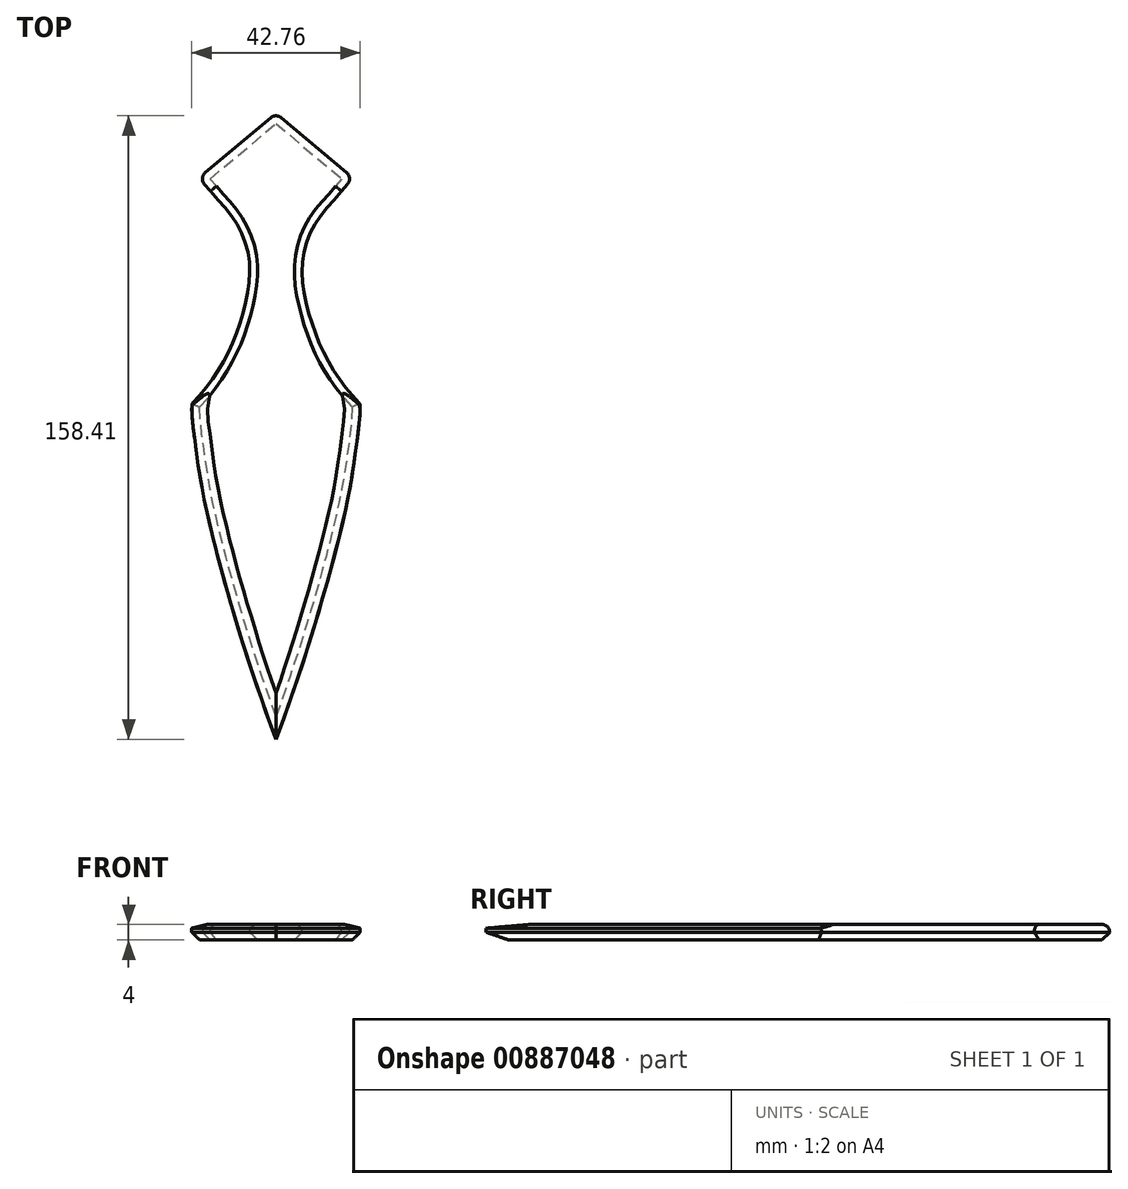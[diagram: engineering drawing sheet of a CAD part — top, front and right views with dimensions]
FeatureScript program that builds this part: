
annotation { "Feature Type Name" : "Feature", "Feature Type Description" : "" }
export const myFeature = defineFeature(function(context is Context, id is Id, definition is map)
    precondition{}
    {
        {
            var Q0;
            Q0=qCreatedBy(makeId("Top.planeOp"),FACE);
            var sketch = newSketch(context, id + "F0", { "sketchPlane" : qUnion([Q0])});
            skLineSegment(sketch, "E0", {"start": v(0, 73.74) * mm, "end": v(19.51, 57.36) * mm});
            skFitSpline(sketch, "E1", {"points": [v(21.28, 0) * mm, v(20.35, -11.32) * mm, v(18.64, -22.28) * mm, v(15.2, -37.21) * mm, v(9.92, -55.97) * mm, v(0, -85.29) * mm], "startDerivative": vector(6.55, -38.74) * mm, "endDerivative": vector(-49.45, -132.4) * mm});
            skLineSegment(sketch, "E2.MirrorCS", {"start": v(0, 73.74) * mm, "end": v(-19.51, 57.36) * mm});
            skFitSpline(sketch, "E3.MirrorCS", {"points": [v(-21.28, 0) * mm, v(-20.35, -11.32) * mm, v(-18.64, -22.28) * mm, v(-15.2, -37.21) * mm, v(-9.92, -55.97) * mm, v(0, -85.29) * mm], "startDerivative": vector(-6.55, -38.74) * mm, "endDerivative": vector(49.45, -132.4) * mm});
            skLineSegment(sketch, "E4", {"start": v(19.51, 57.36) * mm, "end": v(15.6, 57.36) * mm});
            skLineSegment(sketch, "E5", {"start": v(19.51, 57.36) * mm, "end": v(16.67, 53.97) * mm});
            skFitSpline(sketch, "E6", {"points": [v(16.67, 53.97) * mm, v(15.24, 52.32) * mm, v(10.12, 45.98) * mm, v(6.8, 36.24) * mm, v(7.63, 25.91) * mm, v(11.54, 14.16) * mm, v(16.67, 5.5) * mm, v(21.28, 0) * mm], "startDerivative": vector(-14.55, -18.2) * mm, "endDerivative": vector(34.92, -38.87) * mm});
            skLineSegment(sketch, "E7.MirrorCS", {"start": v(-19.51, 57.36) * mm, "end": v(-16.67, 53.97) * mm});
            skFitSpline(sketch, "E8.MirrorCS", {"points": [v(-16.67, 53.97) * mm, v(-15.24, 52.32) * mm, v(-10.12, 45.98) * mm, v(-6.8, 36.24) * mm, v(-7.63, 25.91) * mm, v(-11.54, 14.16) * mm, v(-16.67, 5.5) * mm, v(-21.28, 0) * mm], "startDerivative": vector(14.55, -18.2) * mm, "endDerivative": vector(-34.92, -38.87) * mm});
            skSolve(sketch);
        }
        {
            var Q0;
            Q0 = qSketchRegion(id + "F0", true);
            extrude(context, id + "F1", {"entities" : qUnion([Q0]), "depth" : 4 * mm, "offsetDistance" : 25 * mm});
        }
        {
            var Q0;
            Q0=makeQuery(id+"F1.opExtrude","SWEPT_EDGE",EDGE,{"disambiguationData":[OSD([sQuery(id+"F0.wireOp",EDGE,"E0"),sQuery(id+"F0.wireOp",EDGE,"E2.MirrorCS")])]});
            var Q1;
            Q1=makeQuery(id+"F1.opExtrude","SWEPT_EDGE",EDGE,{"disambiguationData":[OSD([sQuery(id+"F0.wireOp",EDGE,"E0"),sQuery(id+"F0.wireOp",EDGE,"E5")])]});
            var Q2;
            Q2=makeQuery(id+"F1.opExtrude","SWEPT_EDGE",EDGE,{"disambiguationData":[OSD([sQuery(id+"F0.wireOp",EDGE,"E2.MirrorCS"),sQuery(id+"F0.wireOp",EDGE,"E7.MirrorCS")])]});
            fillet(context, id + "F2", {"entities" : qUnion([Q0, Q1, Q2]), "tangentPropagation" : true, "radius" : 2 * mm, "defaultsChanged" : false, "vertexSettings" : [], "allowEdgeOverflow" : false});
        }
        {
            var Q0;
            Q0=makeQuery(id+"F1.opExtrude","CAP_FACE",FACE,{"disambiguationData":[OSD([sQuery(id+"F0.wireOp",EDGE,"E0"),sQuery(id+"F0.wireOp",EDGE,"223ab6cf-2717-4cb8-a3a4-93abdf2f02d5"),sQuery(id+"F0.wireOp",EDGE,"E1"),sQuery(id+"F0.wireOp",EDGE,"E2.MirrorCS"),sQuery(id+"F0.wireOp",EDGE,"08c7ee87-7280-4ebf-840d-ba22bd77c0a61.MirrorCS"),sQuery(id+"F0.wireOp",EDGE,"E3.MirrorCS")])],"isStart":true});
            chamfer(context, id + "F3", {"entities" : qUnion([Q0]), "width" : 2 * mm, "tangentPropagation" : true});
        }
        {
            var Q0;
            Q0=makeQuery(id+"F1.opExtrude","CAP_EDGE",EDGE,{"disambiguationData":[OSD([sQuery(id+"F0.wireOp",EDGE,"E1")])],"isStart":false});
            var Q1;
            Q1=makeQuery(id+"F1.opExtrude","CAP_EDGE",EDGE,{"disambiguationData":[OSD([sQuery(id+"F0.wireOp",EDGE,"E3.MirrorCS")])],"isStart":false});
            chamfer(context, id + "F4", {"entities" : qUnion([Q0, Q1]), "chamferType" : ChamferType.TWO_OFFSETS, "width1" : 1 * mm, "oppositeDirection" : false, "width2" : 4 * mm, "tangentPropagation" : true});
        }
        {
            var Q0;
            Q0=makeQuery(id+"F1.opExtrude","CAP_EDGE",EDGE,{"disambiguationData":[OSD([sQuery(id+"F0.wireOp",EDGE,"E6")])],"isStart":false});
            var Q1;
            {var subQ0=sQuery(id+"F0.wireOp",EDGE,"E5");var subQ1=sQuery(id+"F0.wireOp",EDGE,"E0");Q1=makeQuery(id+"F2.opFillet","BLEND_EDGE",EDGE,{"blendedFrom":[makeQuery(id+"F1.opExtrude","SWEPT_EDGE",EDGE,{"disambiguationData":[OSD([subQ1,subQ0])]}),makeQuery(id+"F1.opExtrude","CAP_FACE",FACE,{"disambiguationData":[OSD([subQ1,sQuery(id+"F0.wireOp",EDGE,"E1"),sQuery(id+"F0.wireOp",EDGE,"E2.MirrorCS"),sQuery(id+"F0.wireOp",EDGE,"E3.MirrorCS"),subQ0,sQuery(id+"F0.wireOp",EDGE,"E6"),sQuery(id+"F0.wireOp",EDGE,"E7.MirrorCS"),sQuery(id+"F0.wireOp",EDGE,"E8.MirrorCS")])],"isStart":false})],"blendedInto":[makeQuery(id+"F1.opExtrude","CAP_FACE",FACE,{"disambiguationData":[OSD([subQ1,sQuery(id+"F0.wireOp",EDGE,"E1"),sQuery(id+"F0.wireOp",EDGE,"E2.MirrorCS"),sQuery(id+"F0.wireOp",EDGE,"E3.MirrorCS"),subQ0,sQuery(id+"F0.wireOp",EDGE,"E6"),sQuery(id+"F0.wireOp",EDGE,"E7.MirrorCS"),sQuery(id+"F0.wireOp",EDGE,"E8.MirrorCS")])],"isStart":false})]});}
            fillet(context, id + "F5", {"entities" : qUnion([Q0, Q1]), "tangentPropagation" : true, "radius" : 2 * mm, "defaultsChanged" : false, "vertexSettings" : [], "allowEdgeOverflow" : false});
        }
    });
